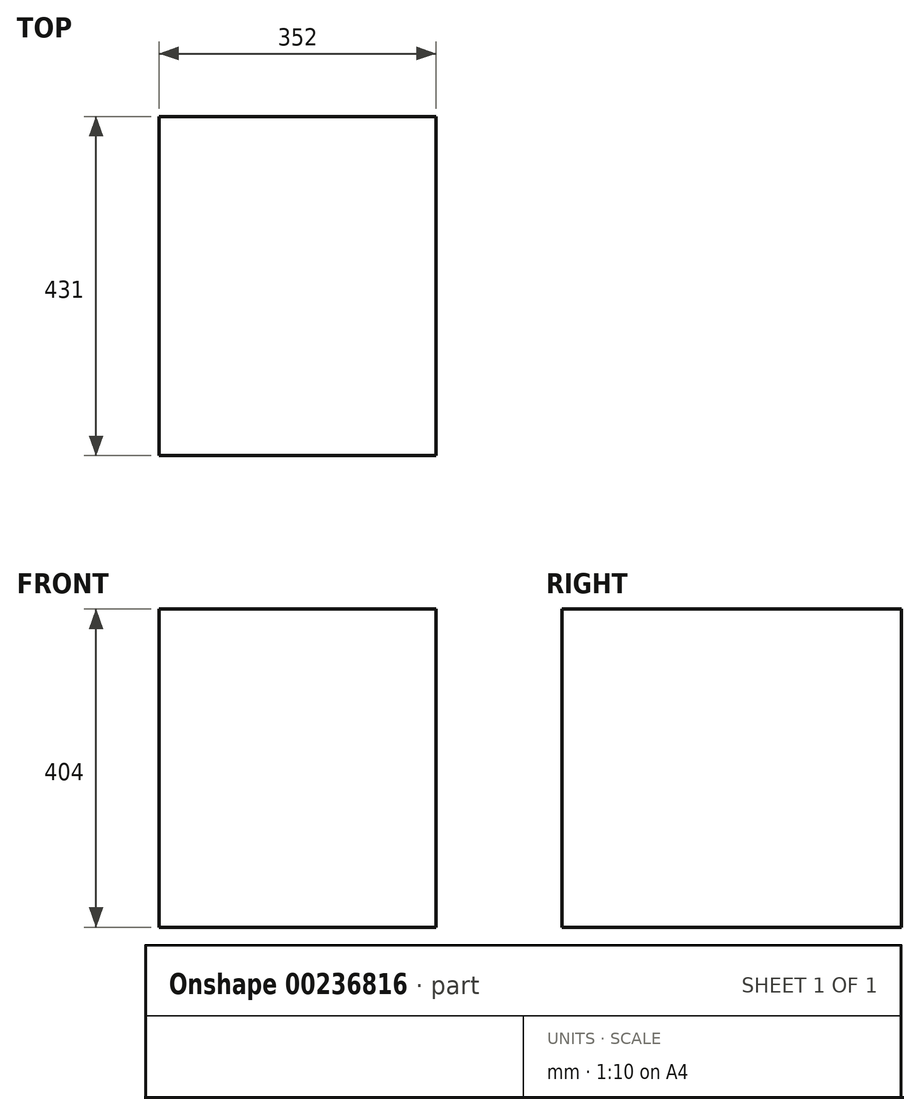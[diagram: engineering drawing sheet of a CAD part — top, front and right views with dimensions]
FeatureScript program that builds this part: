
annotation { "Feature Type Name" : "Feature", "Feature Type Description" : "" }
export const myFeature = defineFeature(function(context is Context, id is Id, definition is map)
    precondition{}
    {
        {
            var Q0;
            Q0=qCreatedBy(makeId("Top.planeOp"),FACE);
            var sketch = newSketch(context, id + "F0", { "sketchPlane" : qUnion([Q0])});
            skLineSegment(sketch, "E0.bottom", {"start": v(-176, 215.5) * mm, "end": v(176, 215.5) * mm});
            skLineSegment(sketch, "E0.top", {"start": v(-176, -215.5) * mm, "end": v(176, -215.5) * mm});
            skLineSegment(sketch, "E0.left", {"start": v(-176, 215.5) * mm, "end": v(-176, -215.5) * mm});
            skLineSegment(sketch, "E0.right", {"start": v(176, 215.5) * mm, "end": v(176, -215.5) * mm});
            skPoint(sketch, "E0.middle", {"position": v(0, 0) * mm});
            skSolve(sketch);
        }
        {
            var Q0;
            Q0=makeQuery(id+"F0.imprint","IMPRINT",FACE,{"disambiguationData":[TD([[makeQuery(id+"F0.imprint","IMPRINT",EDGE,{"derivedFrom":sQuery(id+"F0.wireOp",EDGE,"E0.bottom")}),-1.0]])]});
            extrude(context, id + "F1", {"entities" : qUnion([Q0]), "depth" : 404 * mm});
        }
    });
